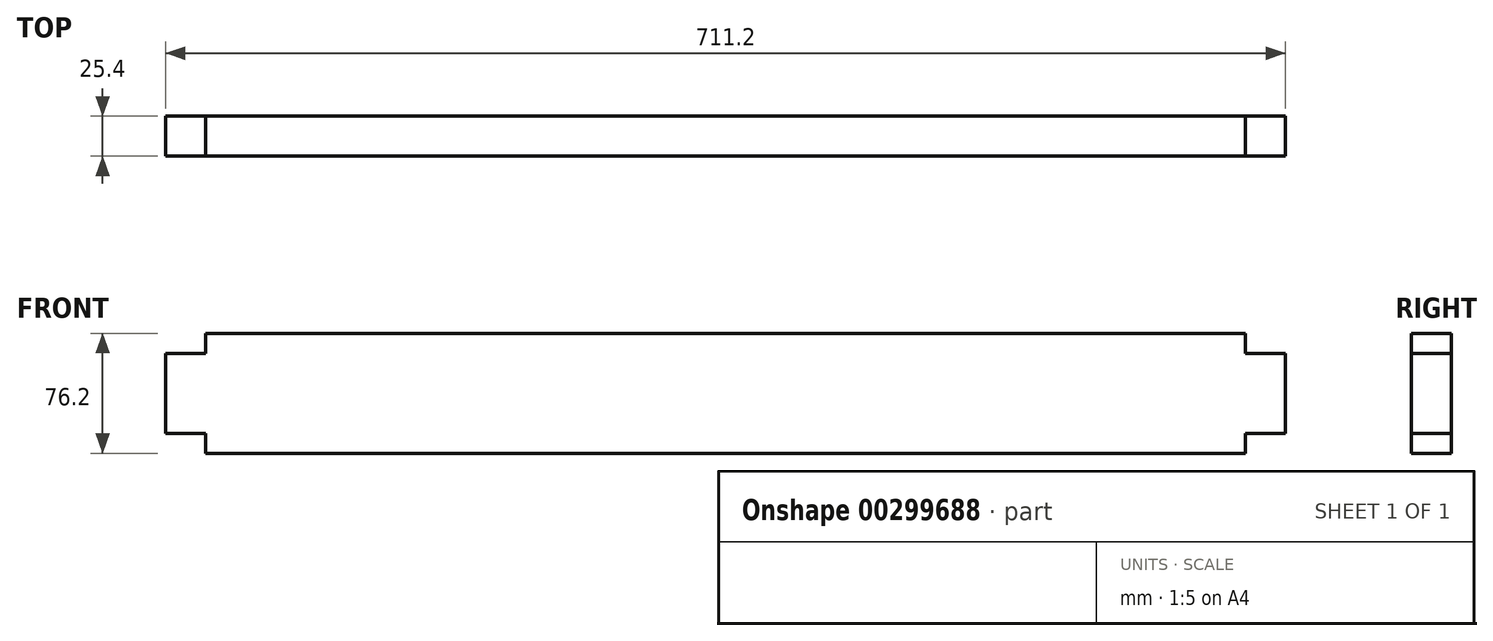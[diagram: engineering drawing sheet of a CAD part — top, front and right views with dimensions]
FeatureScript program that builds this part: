
annotation { "Feature Type Name" : "Feature", "Feature Type Description" : "" }
export const myFeature = defineFeature(function(context is Context, id is Id, definition is map)
    precondition{}
    {
        {
            var Q0;
            Q0=qCreatedBy(makeId("Front.planeOp"),FACE);
            var sketch = newSketch(context, id + "F0", { "sketchPlane" : qUnion([Q0])});
            skLineSegment(sketch, "E0.bottom", {"start": v(-122.6, 37.8) * mm, "end": v(537.8, 37.8) * mm});
            skLineSegment(sketch, "E0.top", {"start": v(-122.6, -38.4) * mm, "end": v(537.8, -38.4) * mm});
            skLineSegment(sketch, "E0.left", {"start": v(-122.6, 37.8) * mm, "end": v(-122.6, -38.4) * mm});
            skLineSegment(sketch, "E0.right", {"start": v(537.8, 37.8) * mm, "end": v(537.8, -38.4) * mm});
            skLineSegment(sketch, "E1.bottom", {"start": v(537.8, -25.7) * mm, "end": v(563.2, -25.7) * mm});
            skLineSegment(sketch, "E1.top", {"start": v(537.8, 25.1) * mm, "end": v(563.2, 25.1) * mm});
            skLineSegment(sketch, "E1.left", {"start": v(537.8, -25.7) * mm, "end": v(537.8, 25.1) * mm});
            skLineSegment(sketch, "E1.right", {"start": v(563.2, -25.7) * mm, "end": v(563.2, 25.1) * mm});
            skLineSegment(sketch, "E2.bottom", {"start": v(-122.6, 25.1) * mm, "end": v(-148, 25.1) * mm});
            skLineSegment(sketch, "E2.top", {"start": v(-122.6, -25.7) * mm, "end": v(-148, -25.7) * mm});
            skLineSegment(sketch, "E2.left", {"start": v(-122.6, 25.1) * mm, "end": v(-122.6, -25.7) * mm});
            skLineSegment(sketch, "E2.right", {"start": v(-148, 25.1) * mm, "end": v(-148, -25.7) * mm});
            skSolve(sketch);
        }
        {
            var Q0;
            Q0=qSketchRegion(id+"F0",true);
            extrude(context, id + "F1", {"entities" : qUnion([Q0]), "depth" : 25.4 * mm});
        }
    });
